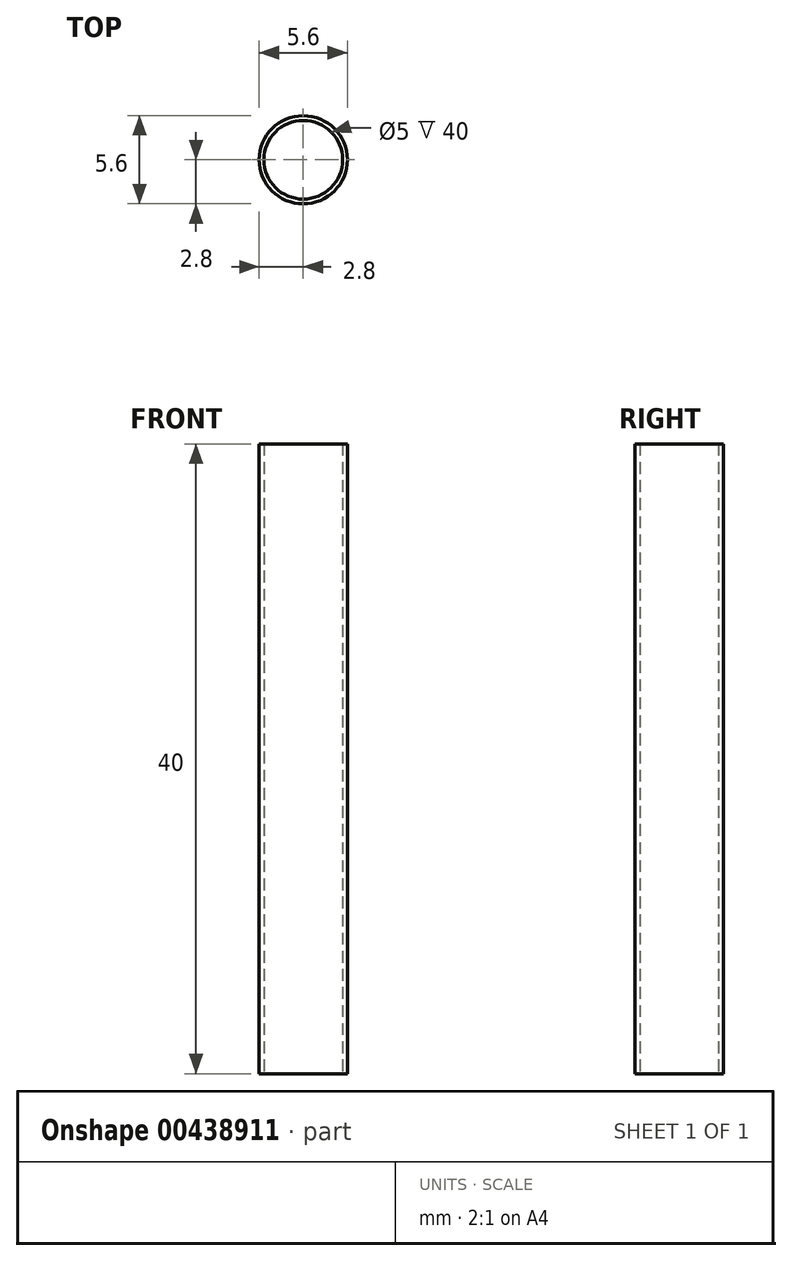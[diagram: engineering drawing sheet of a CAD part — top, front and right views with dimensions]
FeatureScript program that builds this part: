
annotation { "Feature Type Name" : "Feature", "Feature Type Description" : "" }
export const myFeature = defineFeature(function(context is Context, id is Id, definition is map)
    precondition{}
    {
        {
            var Q0;
            Q0=qCreatedBy(makeId("Top.planeOp"),FACE);
            var sketch = newSketch(context, id + "F0", { "sketchPlane" : qUnion([Q0])});
            skCircle(sketch, "E0", {"center": v(0, 0) * mm, "radius": 2.8 * mm});
            skCircle(sketch, "E1", {"center": v(0, 0) * mm, "radius": 2.5 * mm});
            skSolve(sketch);
        }
        {
            var Q0;
            Q0 = qSketchRegion(id + "F0", true);
            extrude(context, id + "F1", {"entities" : qUnion([Q0]), "depth" : 40 * mm});
        }
    });
